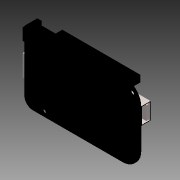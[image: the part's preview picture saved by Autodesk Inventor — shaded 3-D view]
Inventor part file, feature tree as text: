
AUTODESK INVENTOR PART (.ipt)
format: ipt  version: 2014 (Build 180170000, 170)  size: 601,088 bytes
history: native  units: mm
features: fillet x1, other x1, imported_body x1
ambient origin geometry x8: Origin, YZ Plane, XZ Plane, XY Plane, X Axis, Y Axis, Z Axis, Center Point
bodies: Body1 (feature_tree)
feature tree (3):
  fillet  "Fillet1"  [1 undecoded]
  other  "Rough BeagleBone Black1"
  imported_body  "Base1"
note: 1 required parameter value undecoded (feature->parameter linkage not recoverable at this tier; creation-order binding heuristic only, values carry confidence <= 0.55)
